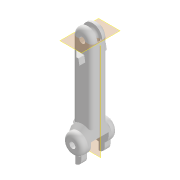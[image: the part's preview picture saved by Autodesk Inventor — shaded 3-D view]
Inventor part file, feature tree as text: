
AUTODESK INVENTOR PART (.ipt)
format: ipt  version: 2020.2 (Build 242310000, 310)  size: 323,072 bytes
history: native  units: mm
features: sketch x9, extrude x8, mirror x5, chamfer x3, fillet x3, plane x2, revolve x1
ambient origin geometry x8: Origin, YZ Plane, XZ Plane, XY Plane, X Axis, Y Axis, Z Axis, Center Point
bodies: Solid1 (feature_tree)
feature tree (31):
  extrude  "base"  Depth=3.0mm
  extrude  "joint"  Depth=10.0mm
  plane  "Work Plane1"
  mirror  "Mirror1"
  chamfer  "Chamfer1"  Distance=8.0mm
  extrude  "joint_2"  Depth=3.0mm
  fillet  "Fillet2"  Radius=5.0mm
  plane  "Work Plane2"
  revolve  "Revolution2"  [1 undecoded]
  extrude  "Extrusion8"  Depth=2.0mm TaperAngle=45.0deg
  extrude  "Extrusion9"  Depth=2.0mm
  mirror  "Mirror4"
  fillet  "Fillet4"  Radius=3.5mm
  extrude  "Extrusion10"  Depth=40.0mm TaperAngle=0.0deg
  mirror  "Mirror5"
  chamfer  "Chamfer3"  Distance=13.962634mm
  extrude  "lock_1"  Depth=2.0mm
  mirror  "Mirror2"
  chamfer  "Chamfer2"  Distance=3.0mm
  extrude  "lock_2"  Depth=3.0mm TaperAngle=45.0deg
  mirror  "Mirror3"
  fillet  "Fillet3"  Radius=4.0mm
  sketch  "Sketch1"  dims[d0=3.0mm d1=44.0mm]
  sketch  "Sketch2"  dims[d2=3.0mm d3=10.0mm]
  sketch  "Sketch4"  dims[d4=10.0mm d5=8.0mm d6=0.0mm]
  sketch  "Sketch7"  dims[d7=10.0mm d8=3.0mm d9=5.0mm d10=0.0mm]
  sketch  "Sketch8"  dims[d12=10.5mm d13=3.0mm]
  sketch  "Sketch9"  dims[d14=9.0mm d15=0.0mm d16=2.0mm d17=2.0mm d18=45.0deg]
  sketch  "Sketch10"  dims[d19=2.0mm d20=3.5mm d21=3.5mm]
  sketch  "Sketch11"  dims[d23=2.5mm d24=40.0mm d25=0.0mm]
  sketch  "Sketch12"  dims[d32=6.0mm d33=13.962634mm d34=5.0mm d35=3.0mm d36=0.0mm d37=3.0mm d38=2.0mm d39=45.0deg d40=4.0mm d41=3.0mm d42=3.0mm d43=0.0mm d44=3.0mm d45=4.0mm d46=90.0deg d47=3.5mm d48=2.5mm d49=180.0deg d50=5.0mm d51=0.0mm d52=4.0mm d53=3.0mm d54=3.0mm d55=0.0mm d56=3.0mm d57=6.0mm d58=3.0mm d59=13.962634mm d60=3.0mm d61=0.0mm d62=3.0mm d63=2.0mm d64=45.0deg]
note: 1 required parameter value undecoded (feature->parameter linkage not recoverable at this tier; creation-order binding heuristic only, values carry confidence <= 0.55)
